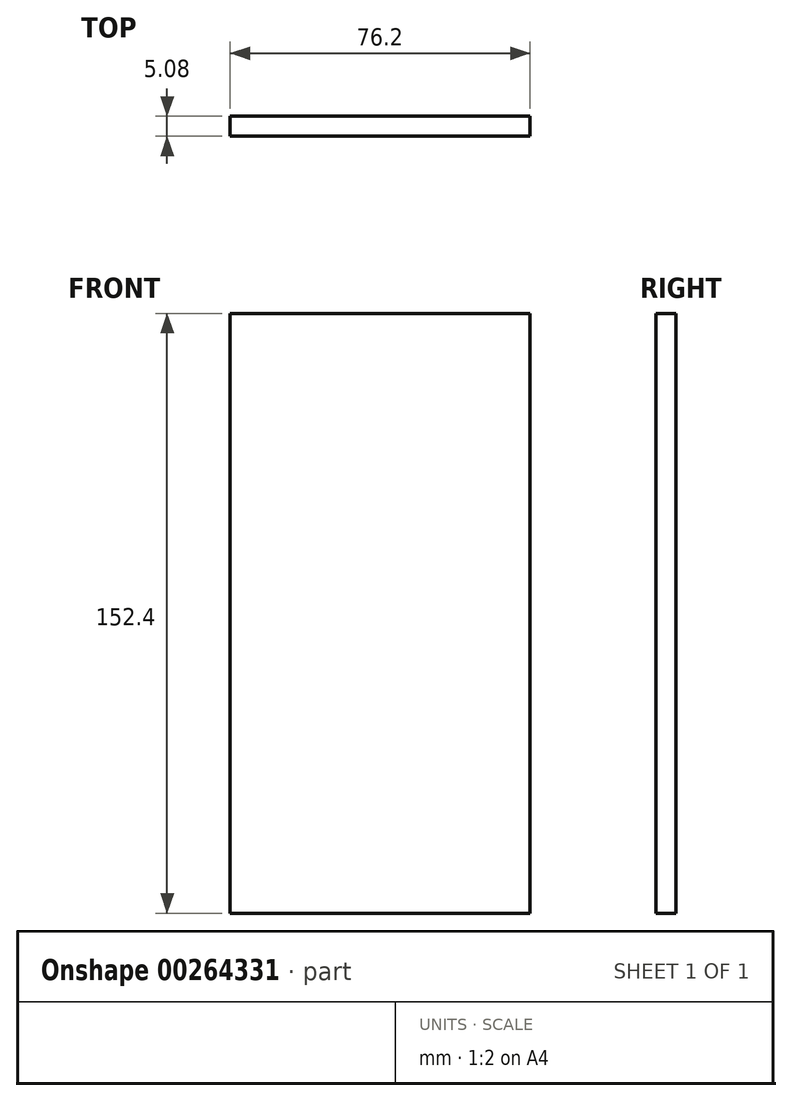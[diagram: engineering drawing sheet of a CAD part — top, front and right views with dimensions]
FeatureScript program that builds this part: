
annotation { "Feature Type Name" : "Feature", "Feature Type Description" : "" }
export const myFeature = defineFeature(function(context is Context, id is Id, definition is map)
    precondition{}
    {
        {
            var Q0;
            Q0=qCreatedBy(makeId("Front.planeOp"),FACE);
            var sketch = newSketch(context, id + "F0", { "sketchPlane" : qUnion([Q0])});
            skLineSegment(sketch, "E0.bottom", {"start": v(-37, -57.15) * mm, "end": v(39.2, -57.15) * mm});
            skLineSegment(sketch, "E0.top", {"start": v(-37, 95.25) * mm, "end": v(39.2, 95.25) * mm});
            skLineSegment(sketch, "E0.left", {"start": v(-37, -57.15) * mm, "end": v(-37, 95.25) * mm});
            skLineSegment(sketch, "E0.right", {"start": v(39.2, -57.15) * mm, "end": v(39.2, 95.25) * mm});
            skSolve(sketch);
        }
        {
            var Q0;
            Q0=makeQuery(id+"F0.imprint","IMPRINT",FACE,{"disambiguationData":[TD([[makeQuery(id+"F0.imprint","IMPRINT",EDGE,{"derivedFrom":sQuery(id+"F0.wireOp",EDGE,"E0.bottom")}),1.0]])]});
            extrude(context, id + "F1", {"entities" : qUnion([Q0]), "depth" : 5.08 * mm});
        }
    });
